FCSTD DOCUMENT  (FreeCAD 0.18R16110 (Git))
Label: rail
License: All rights reserved
LicenseURL: http://en.wikipedia.org/wiki/All_rights_reserved
objects: Part::FeaturePython×9, Part::Cylinder×5
note: 14 computed .brp shape members not serialized (recipe doc carries the construction recipe); baked Part::Feature solids carry a one-line shape summary decoded from their .brp

FEATURE [Part::FeaturePython] b_connector_rail_001_  label="connector-rail_001"  # a2plus imported part (geometry in sourceFile) (typed FeaturePython)
  Placement = pos=(-70,0,0) rot=(0,0,1;0rad)
  a2p_Version = V0.1
  fixedPosition = true
  sourceFile = ./../rail/RailT.FCStd
  subassemblyImport = false
  timeLastImport = 1.55982e+09
  updateColors = true
FEATURE [Part::FeaturePython] b_connector_rail_001_001  label="connector-rail_002"  # a2plus imported part (geometry in sourceFile) (typed FeaturePython)
  Placement = pos=(70,0,2.3e-14) rot=(0,1,0;3.14159rad)
  a2p_Version = V0.1
  fixedPosition = false
  sourceFile = ./../rail/RailT.FCStd
  subassemblyImport = false
  timeLastImport = 1.55982e+09
  updateColors = true
FEATURE [Part::Cylinder] Cylinder
  Angle = 360
  AttacherType = Attacher::AttachEngine3D
  Height = 100
  Placement = pos=(50,600,6.8e-15) rot=(0,-1,0;1.5708rad)
  Radius = 10
FEATURE [Part::Cylinder] Cylinder001
  Angle = 360
  AttacherType = Attacher::AttachEngine3D
  Height = 580
  Placement = pos=(-70,10,3.1e-14) rot=(0.57735,0.57735,0.57735;4.18879rad)
  Radius = 10
FEATURE [Part::Cylinder] Cylinder002
  Angle = 360
  AttacherType = Attacher::AttachEngine3D
  Height = 580
  Placement = pos=(70,10,3.1e-14) rot=(0.57735,0.57735,0.57735;4.18879rad)
  Radius = 10
FEATURE [Part::Cylinder] Cylinder003
  Angle = 360
  AttacherType = Attacher::AttachEngine3D
  Height = 580
  Placement = pos=(0,10,20) rot=(0.57735,0.57735,0.57735;4.18879rad)
  Radius = 10
FEATURE [Part::FeaturePython] b_connector_rail_001_002  label="connector-rail_003"  # a2plus imported part (geometry in sourceFile) (typed FeaturePython)
  Placement = pos=(-70,600,0) rot=(0,0,1;0rad)
  a2p_Version = V0.1
  fixedPosition = true
  sourceFile = ../rail/RailT.FCStd
  subassemblyImport = false
  timeLastImport = 1.55982e+09
  updateColors = true
FEATURE [Part::FeaturePython] b_connector_rail_001_003  label="connector-rail_004"  # a2plus imported part (geometry in sourceFile) (typed FeaturePython)
  Placement = pos=(70,600,2.3e-14) rot=(0,1,0;3.14159rad)
  a2p_Version = V0.1
  fixedPosition = false
  sourceFile = ../rail/RailT.FCStd
  subassemblyImport = false
  timeLastImport = 1.55982e+09
  updateColors = true
FEATURE [Part::Cylinder] Cylinder004
  Angle = 360
  AttacherType = Attacher::AttachEngine3D
  Height = 100
  Placement = pos=(50,0,6.8e-15) rot=(0,-1,0;1.5708rad)
  Radius = 10
FEATURE [Part::FeaturePython] b_RailCenter_001_  label="RailCenter_001"  # a2plus imported part (geometry in sourceFile) (typed FeaturePython)
  Placement = pos=(-4e-15,4e-15,20) rot=(0.57735,0.57735,-0.57735;4.18879rad)
  a2p_Version = V0.1
  fixedPosition = false
  sourceFile = ./../rail/RailCenter.FCStd
  subassemblyImport = false
  timeLastImport = 1.55982e+09
  updateColors = true
FEATURE [Part::FeaturePython] b_RailCenter_001_001  label="RailCenter_002"  # a2plus imported part (geometry in sourceFile) (typed FeaturePython)
  Placement = pos=(-4e-15,600,20) rot=(0.57735,0.57735,-0.57735;4.18879rad)
  a2p_Version = V0.1
  fixedPosition = false
  sourceFile = ./../rail/RailCenter.FCStd
  subassemblyImport = false
  timeLastImport = 1.55982e+09
  updateColors = true
FEATURE [Part::FeaturePython] b_Rack_001_  label="Rack_001"  # a2plus imported part (geometry in sourceFile) (typed FeaturePython)
  Placement = pos=(-1e-15,-5,30) rot=(0,-1,0;1.5708rad)
  a2p_Version = V0.1
  fixedPosition = false
  sourceFile = ./../rail/Rack.FCStd
  subassemblyImport = false
  timeLastImport = 1.56013e+09
  updateColors = true
FEATURE [Part::FeaturePython] b_Rack_001_001  label="Rack_002"  # a2plus imported part (geometry in sourceFile) (typed FeaturePython)
  Placement = pos=(-1e-15,195,30) rot=(0,-1,0;1.5708rad)
  a2p_Version = V0.1
  fixedPosition = false
  sourceFile = ./../rail/Rack.FCStd
  subassemblyImport = false
  timeLastImport = 1.56013e+09
  updateColors = true
FEATURE [Part::FeaturePython] b_Rack_001_002  label="Rack_003"  # a2plus imported part (geometry in sourceFile) (typed FeaturePython)
  Placement = pos=(-1e-15,395,30) rot=(0,-1,0;1.5708rad)
  a2p_Version = V0.1
  fixedPosition = false
  sourceFile = ./../rail/Rack.FCStd
  subassemblyImport = false
  timeLastImport = 1.56013e+09
  updateColors = true
